# Revit family: otkatnie_protivopozarnie_vorota_firetechnics-p_ei60_ei90
name_source: partatom
category: Двери
revit_build: Autodesk Revit 2016 (Build: 20150714_1515(x64)
units: mm (PartAtom-declared; Revit-internal decimal feet)

## family parameters
Всегда вертикально = Да
Общий = Нет
Основа = Стена
При загрузке вырезать с полостями = Нет
Точка расчета площади = Нет

## types (2) — shared parameters
ADSK_URL страницы изделия = https://www.fire-tec.ru
ADSK_Завод-изготовитель = Firetechnics
ADSK_Размер_Высота = 3000 мм
URL = https://www.fire-tec.ru
Аналитическая конструкция = <Нет>
Высота противопожарной двери = 2000 мм
Высота створки = 3000 мм
Изготовитель = Firetechnics
Материал полотна = Полотно с наполнителем из минерального заполнителя для ворот
Материал профиля = Сталь_оцинкованная_листовая
Материал ручки = Пластмасса, непрозрачная, черная
Толщина полотна ворот = 60 мм
Ширина противопожарной двери = 800 мм

## per-type parameters (varying)
| type | ADSK_Наименование | ADSK_Предел огнестойкости | ADSK_Размер_Ширина | Вторая створка | Второй рельс | Крепеж 2 | Крепеж1 | Ловушка ворот | Огнестойкость | УГО | УГО2 | Ширина 2 створки | Ширина второго рельса | Ширина створок | второй рельс |
| Откатные противопажарные ворота 3x3 EI90 | Откатные противопожарные ворота модели FireTechnics-P EI90 | EI90 | 3000 мм | 5 мм | 205 мм | 0 мм | 0 мм | 130 мм | EI60 | 1 мм | 3000 мм | 30 мм | 40 мм | 3000 мм | 59 мм |
| Откатные противопажарные ворота 6x3 EI120 | Откатные противопожарные ворота модели FireTechnics-P EI120 | EI120 | 6000 мм | 3200 мм | 12550 мм | 800 мм | 800 мм | 240 мм | EI120 | 3000 мм | 4000 мм | 100 мм | 60 мм | 6000 мм | 125 мм |

## geometry (parser evidence)
native form markers: Blend x2
no freeform markers — native parametric forms only
